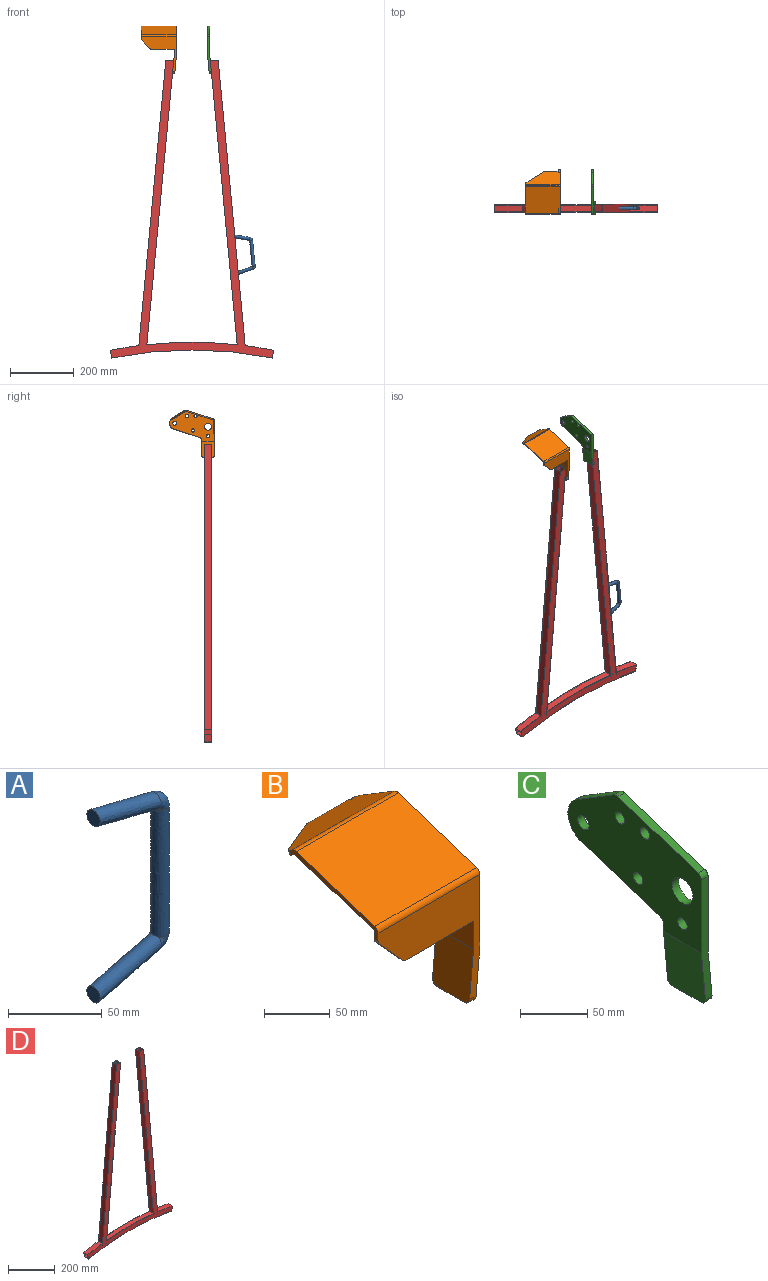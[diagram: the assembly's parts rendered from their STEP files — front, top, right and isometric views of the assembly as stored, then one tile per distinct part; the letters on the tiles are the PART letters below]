
ASSEMBLY  parts=4 mates=3
PART A: 9 faces, bbox 56.2x21.4x126.4 mm
  f0: plane 11.39x11.39mm, normal (-1,0,0), area 78.5mm2, adj f1
  f1: bspline ~46.21x21.55mm, area 1473.7mm2, adj f0,f2,f8
  f2: bspline ~20x11.06mm, area 189.3mm2, adj f1,f3,f8
  f3: bspline ~84.61x9.83mm, area 2545.2mm2, adj f2,f4,f6,f7,f8
  f4: bspline ~46.21x21.55mm, area 1477.1mm2, adj f3,f5,f7
  f5: plane 11.39x11.39mm, normal (-1,0,0), area 78.5mm2, adj f4
  f6: bspline ~10x4.84mm, area 0mm2, adj f3,f7
  f7: bspline ~10.77x9.85mm, area 189.3mm2, adj f3,f4,f6
  f8: bspline ~10x4.84mm, area 20.6mm2, adj f1,f2,f3
PART B: 35 faces, bbox 110x140.9x149.4 mm
  f0: plane 110x42.68mm, normal (0,0.52,0.85), area 4198.3mm2, adj f5,f8,f16,f19,f26,f27,f30,f31
  f1: plane 103x43.07mm, normal (0,-0.52,-0.85), area 3926.1mm2, adj f5,f9,f27,f28,f30,f31,f32
  f2: plane 111.83x110mm, normal (0,-1,0), area 4470.2mm2, adj f3,f5,f6,f7,f8,f9,f14,f17
  f3: plane 72.79x4mm, normal (0,0,-1), area 291.2mm2, adj f2,f4,f9,f34
  f4: plane 103x40.73mm, normal (0,1,0), area 3763.1mm2, adj f3,f5,f9,f28,f29,f33,f34
  f5: plane 95.47x39.87mm, normal (-1,0,0), area 425.7mm2, adj f0,f1,f2,f4,f12,f14,f16,f28
  f6: plane 49.78x40mm, normal (-1,0,0.09), area 1989.3mm2, adj f2,f9,f10,f11,f17,f18
  f7: plane 50.11x40mm, normal (1,0,-0.09), area 2002.5mm2, adj f2,f8,f10,f11,f17,f18
  f8: plane 140.85x99.26mm, normal (1,0,0), area 8376.5mm2, adj f0,f2,f7,f11,f12,f13,f14,f15
  f9: plane 140.85x95.03mm, normal (-1,0,0), area 7622.4mm2, adj f1,f2,f3,f4,f6,f11,f13,f15
  f10: plane 30x6.97mm, normal (-0.09,0,-1), area 210mm2, adj f6,f7,f17,f18
  f11: plane 51.83x11.24mm, normal (0,1,0), area 361.9mm2, adj f6,f7,f8,f9,f15,f18
  f12: plane 110x84.7mm, normal (0,-0.31,0.95), area 9797.5mm2, adj f5,f8,f14,f16
  f13: plane 83.59x27.2mm, normal (0,0.31,-0.95), area 615.3mm2, adj f8,f9,f15,f19
  f14: cylinder r=5mm len=110mm, axis (-1,0,0), area 690.9mm2, adj f2,f5,f8,f12
  f15: cylinder r=5mm len=7mm, axis (1,0,0), area 44mm2, adj f8,f9,f11,f13
  f16: cylinder r=5mm len=110mm, axis (-1,0,0), area 474.4mm2, adj f0,f5,f8,f12
  f17: cylinder r=5mm len=7.44mm, axis (1,0,-0.09), area 55mm2, adj f2,f6,f7,f10
  f18: cylinder r=5mm len=7.44mm, axis (-1,0,0.09), area 55mm2, adj f6,f7,f10,f11
  f19: cylinder r=20mm len=36.09mm, axis (1,0,0), area 319.1mm2, adj f0,f8,f9,f13,f26
  f20: cylinder r=11mm len=22mm, axis (1,0,0), area 483.8mm2, adj f8,f9
  f21: cylinder r=5mm len=10mm, axis (1,0,0), area 219.9mm2, adj f8,f9
  f22: cylinder r=5mm len=10mm, axis (1,0,0), area 219.9mm2, adj f8,f9
  f23: cylinder r=6mm len=12mm, axis (1,0,0), area 263.9mm2, adj f8,f9
  f24: cylinder r=5mm len=10mm, axis (1,0,0), area 219.9mm2, adj f8,f9
  f25: cylinder r=5mm len=10mm, axis (1,0,0), area 219.9mm2, adj f8,f9
  f26: plane 3.71x2.67mm, normal (1,0,0), area 0.7mm2, adj f0,f19,f27
  f27: plane 43.32x3.41mm, normal (0,0.85,-0.52), area 173.3mm2, adj f0,f1,f9,f26,f31
  f28: plane 103x85.82mm, normal (0,0.31,-0.95), area 9296.2mm2, adj f1,f4,f5,f9
  f29: plane 27.69x25.21mm, normal (-0.74,0,-0.67), area 149.8mm2, adj f2,f4,f33,f34
  f30: plane 54.68x37.33mm, normal (-0.6,0.68,-0.42), area 274.1mm2, adj f0,f1,f31,f32
  f31: cylinder r=5mm len=3.94mm, axis (0,-0.52,-0.85), area 12.9mm2, adj f0,f1,f27,f30
  f32: cylinder r=5mm len=5.49mm, axis (0,0.52,0.85), area 18.5mm2, adj f0,f1,f5,f30
  f33: cylinder r=5mm len=4mm, axis (0,-1,0), area 14.8mm2, adj f2,f4,f5,f29
  f34: cylinder r=5mm len=4mm, axis (0,1,0), area 16.6mm2, adj f2,f3,f4,f29
PART C: 22 faces, bbox 11.7x140.9x149 mm
  f0: plane 140.85x98.93mm, normal (1,0,0), area 8363.2mm2, adj f1,f3,f5,f7,f8,f9,f10,f11
  f1: plane 49.45x40mm, normal (1,0,0.09), area 1976mm2, adj f0,f3,f5,f6,f13,f14
  f2: plane 49.78x40mm, normal (-1,0,-0.09), area 1989.3mm2, adj f3,f4,f5,f6,f13,f14
  f3: plane 111.5x11.21mm, normal (0,-1,0), area 779.6mm2, adj f0,f1,f2,f4,f10,f13
  f4: plane 140.85x99.26mm, normal (-1,0,0), area 8376.5mm2, adj f2,f3,f5,f7,f8,f9,f10,f11
  f5: plane 51.5x11.21mm, normal (0,1,0), area 359.6mm2, adj f0,f1,f2,f4,f12,f14
  f6: plane 30x6.97mm, normal (0.09,0,-1), area 210mm2, adj f1,f2,f13,f14
  f7: plane 84.7x27.56mm, normal (0,-0.31,0.95), area 623.5mm2, adj f0,f4,f10,f11
  f8: plane 38.97x23.78mm, normal (0,0.52,0.85), area 319.6mm2, adj f0,f4,f11,f15
  f9: plane 83.59x27.2mm, normal (0,0.31,-0.95), area 615.3mm2, adj f0,f4,f12,f15
  f10: cylinder r=5mm len=7mm, axis (-1,0,0), area 44mm2, adj f0,f3,f4,f7
  f11: cylinder r=5mm len=7mm, axis (1,0,0), area 30.2mm2, adj f0,f4,f7,f8
  f12: cylinder r=5mm len=7mm, axis (-1,0,0), area 44mm2, adj f0,f4,f5,f9
  f13: cylinder r=5mm len=7.44mm, axis (1,0,0.09), area 55mm2, adj f1,f2,f3,f6
  f14: cylinder r=5mm len=7.44mm, axis (1,0,0.09), area 55mm2, adj f1,f2,f5,f6
  f15: cylinder r=20mm len=36.09mm, axis (-1,0,0), area 319.1mm2, adj f0,f4,f8,f9
  f16: cylinder r=6mm len=12mm, axis (1,0,0), area 263.9mm2, adj f0,f4
  f17: cylinder r=5mm len=10mm, axis (1,0,0), area 219.9mm2, adj f0,f4
  f18: cylinder r=5mm len=10mm, axis (1,0,0), area 219.9mm2, adj f0,f4
  f19: cylinder r=5mm len=10mm, axis (1,0,0), area 219.9mm2, adj f0,f4
  f20: cylinder r=11mm len=22mm, axis (1,0,0), area 483.8mm2, adj f0,f4
  f21: cylinder r=5mm len=10mm, axis (1,0,0), area 219.9mm2, adj f0,f4
PART D: 44 faces, bbox 514.6x25x936.5 mm
  f0: plane 513.85x45.88mm, normal (0,-1,0), area 10486.8mm2, adj f2,f3,f5,f6,f12,f13,f14,f15
  f1: cylinder r=1299.88mm len=284.34mm, axis (0,1,0), area 7122.7mm2, adj f8,f10,f27,f40
  f2: cylinder r=1297.92mm len=21.24mm, axis (0,1,0), area 449.3mm2, adj f0,f7,f30,f34
  f3: cylinder r=1297.92mm len=284.72mm, axis (0,1,0), area 5991.1mm2, adj f0,f7,f17,f33
  f4: cylinder r=1299.88mm len=89.85mm, axis (0,1,0), area 2277.4mm2, adj f8,f10,f14,f26
  f5: cylinder r=1297.92mm len=21.24mm, axis (0,1,0), area 449.3mm2, adj f0,f7,f16,f20
  f6: cylinder r=1297.92mm len=89.28mm, axis (0,1,0), area 1900.8mm2, adj f0,f7,f14,f19
  f7: plane 513.85x45.88mm, normal (0,1,0), area 10486.8mm2, adj f2,f3,f5,f6,f12,f13,f14,f15
  f8: plane 936.5x514.61mm, normal (0,1,0), area 57381.6mm2, adj f1,f4,f9,f11,f14,f15,f26,f27
  f9: cylinder r=1299.88mm len=89.85mm, axis (0,1,0), area 2277.4mm2, adj f8,f10,f15,f41
  f10: plane 936.5x514.61mm, normal (0,-1,0), area 57381.6mm2, adj f1,f4,f9,f11,f14,f15,f26,f27
  f11: cylinder r=1275.37mm len=505mm, axis (0,1,0), area 12709mm2, adj f8,f10,f14,f15
  f12: cylinder r=1277.33mm len=505.77mm, axis (0,1,0), area 10691.8mm2, adj f0,f7,f14,f15
  f13: cylinder r=1297.92mm len=89.28mm, axis (0,1,0), area 1900.8mm2, adj f0,f7,f15,f31
  f14: plane 25x24.04mm, normal (-0.98,0,-0.2), area 180.4mm2, adj f0,f4,f6,f7,f8,f10,f11,f12
  f15: plane 25x24.04mm, normal (0.98,0,-0.2), area 180.4mm2, adj f0,f7,f8,f9,f10,f11,f12,f13
  f16: plane 21x11.68mm, normal (-1,0,0.09), area 246.4mm2, adj f0,f5,f7,f18
  f17: plane 21x11.9mm, normal (1,0,-0.09), area 251.1mm2, adj f0,f3,f7,f18
  f18: plane 21x2mm, normal (0,0,-1), area 42mm2, adj f0,f7,f16,f17
  f19: plane 21x8.86mm, normal (-1,0,0.09), area 186.9mm2, adj f0,f6,f7,f21
  f20: plane 21x9.13mm, normal (1,0,-0.09), area 192.5mm2, adj f0,f5,f7,f21
  f21: plane 21x2mm, normal (0,0,-1), area 42mm2, adj f0,f7,f19,f20
  f22: plane 897.31x105.93mm, normal (0,1,0), area 18816.2mm2, adj f23,f25,f28,f29
  f23: plane 897.31x84.93mm, normal (1,0,-0.09), area 18927.8mm2, adj f22,f24,f28,f29
  f24: plane 897.31x105.93mm, normal (0,-1,0), area 18816.2mm2, adj f23,f25,f28,f29
  f25: plane 894.77x84.69mm, normal (-1,0,0.09), area 18874.1mm2, adj f22,f24,f28,f29
  f26: plane 897.58x84.96mm, normal (-1,0,0.09), area 22539.7mm2, adj f4,f8,f10,f28
  f27: plane 894.54x84.67mm, normal (1,0,-0.09), area 22463.5mm2, adj f1,f8,f10,f28
  f28: plane 25x25mm, normal (0,0,1), area 184mm2, adj f8,f10,f22,f23,f24,f25,f26,f27
  f29: cylinder r=1299.88mm len=21.24mm, axis (0,1,0), area 449.3mm2, adj f22,f23,f24,f25
  f30: plane 21x8.6mm, normal (-1,0,-0.09), area 181.4mm2, adj f0,f2,f7,f32
  f31: plane 21x8.34mm, normal (1,0,0.09), area 175.9mm2, adj f0,f7,f13,f32
  f32: plane 21x2mm, normal (0,0,-1), area 42mm2, adj f0,f7,f30,f31
  f33: plane 21x11.38mm, normal (-1,0,-0.09), area 240.1mm2, adj f0,f3,f7,f35
  f34: plane 21x11.16mm, normal (1,0,0.09), area 235.3mm2, adj f0,f2,f7,f35
  f35: plane 21x2mm, normal (0,0,-1), area 42mm2, adj f0,f7,f33,f34
  f36: plane 894.77x84.69mm, normal (1,0,0.09), area 18874.1mm2, adj f37,f39,f42,f43
  f37: plane 897.31x105.93mm, normal (0,-1,0), area 18816.2mm2, adj f36,f38,f42,f43
  f38: plane 897.31x84.93mm, normal (-1,0,-0.09), area 18927.8mm2, adj f37,f39,f42,f43
  f39: plane 897.31x105.93mm, normal (0,1,0), area 18816.2mm2, adj f36,f38,f42,f43
  f40: plane 894.54x84.67mm, normal (-1,0,-0.09), area 22463.5mm2, adj f1,f8,f10,f42
  f41: plane 897.58x84.96mm, normal (1,0,0.09), area 22539.7mm2, adj f8,f9,f10,f42
  f42: plane 25x25mm, normal (0,0,1), area 184mm2, adj f8,f10,f36,f37,f38,f39,f40,f41
  f43: cylinder r=1299.88mm len=21.24mm, axis (0,1,0), area 449.3mm2, adj f36,f37,f38,f39
PLACE A rot(axis=(0,-1,0),5.4deg) t=(-10.48,-80.73,632.67)mm
PLACE B rot(axis=(0,1,0),0deg) t=(231.99,199.27,1196.41)mm
PLACE C rot(axis=(0,-1,0),0deg) t=(-95.84,199.27,1196.08)mm
PLACE D t=(-397.93,-80.73,262.78)mm
MATE fastened C.f1 <-> D.f40  axis (1,0,0.09) through (-84.16,-80.73,1146.96)mm
MATE fastened A.f5 <-> D.f41  axis (-1,0,-0.09) through (0.35,-80.73,518.18)mm
MATE fastened B.f6 <-> D.f27  axis (-1,0,0.09) through (-206.7,-80.73,1146.96)mm
